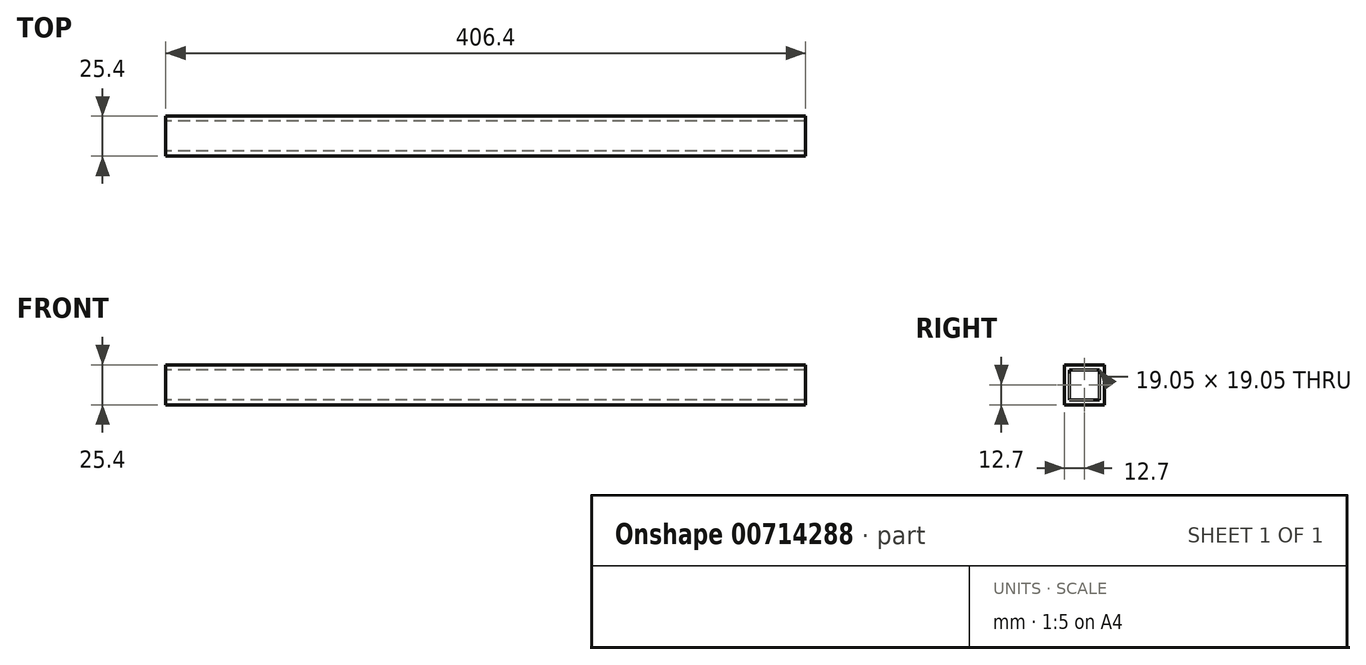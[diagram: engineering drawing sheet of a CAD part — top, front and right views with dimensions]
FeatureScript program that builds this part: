
annotation { "Feature Type Name" : "Feature", "Feature Type Description" : "" }
export const myFeature = defineFeature(function(context is Context, id is Id, definition is map)
    precondition{}
    {
        {
            var Q0;
            Q0=qCreatedBy(makeId("Right.planeOp"),FACE);
            var sketch = newSketch(context, id + "F0", { "sketchPlane" : qUnion([Q0])});
            skLineSegment(sketch, "E0.bottom", {"start": v(12.7, 12.7) * mm, "end": v(-12.7, 12.7) * mm});
            skLineSegment(sketch, "E0.top", {"start": v(12.7, -12.7) * mm, "end": v(-12.7, -12.7) * mm});
            skLineSegment(sketch, "E0.left", {"start": v(12.7, 12.7) * mm, "end": v(12.7, -12.7) * mm});
            skLineSegment(sketch, "E0.right", {"start": v(-12.7, 12.7) * mm, "end": v(-12.7, -12.7) * mm});
            skPoint(sketch, "E0.middle", {"position": v(0, 0) * mm});
            skLineSegment(sketch, "E1.0", {"start": v(-9.53, 9.53) * mm, "end": v(-9.53, -9.52) * mm});
            skLineSegment(sketch, "E1.1", {"start": v(9.52, 9.53) * mm, "end": v(-9.53, 9.53) * mm});
            skLineSegment(sketch, "E1.2", {"start": v(9.53, 9.53) * mm, "end": v(9.53, -9.52) * mm});
            skLineSegment(sketch, "E1.3", {"start": v(9.53, -9.52) * mm, "end": v(-9.53, -9.52) * mm});
            skSolve(sketch);
        }
        {
            var Q0;
            Q0 = qSketchRegion(id + "F0", true);
            extrude(context, id + "F1", {"entities" : qUnion([Q0]), "depth" : 406.4 * mm, "offsetDistance" : 25.4 * mm});
        }
    });
